# Revit family: Gymnasium-Eqpt_Basketball_IPIbybison_IP1345SF
name_source: partatom
category: Specialty Equipment
revit_build: Autodesk Revit 2018 (Build: 20170927_1515(x64)
units: mm (PartAtom-declared; Revit-internal decimal feet)

## family parameters
Always vertical = Yes
Cut with Voids When Loaded = No
Part Type = Normal
Room Calculation Point = No
Round Connector Dimension = Use Diameter
Shared = No

## types (2) — shared parameters
Available Options = as Specified
Backboard Type = Backboard_BA42XLGlass
Manufacturer = IPI by Bison
Manufacturer Fax = 800-638-0698
Manufacturer Website = https://ipibybison.com
Product Data = http://www.arcat.com
Revision = R1_01-2018
Sales Information = https://ipibybison.com
URL = https://ipibybison.com
zero-valued in all types: Expected Lifespan (Years), Maintenance Schedule (Months), Warranty Duration (Years)

## per-type parameters (varying)
| type | Description | Fold Left | Fold Right | Model |
| Right Fold | IPI by Bison Right Side Folding Basketball Frame and Backboard - IP1345SFR 23' as Specified | No | Yes | IP1345SFR 23' |
| Left Fold | IPI by Bison Left Side Folding Basketball Frame and Backboard - IP1345SFL 23' as Specified | Yes | No | IP1345SFL 23' |

## geometry (parser evidence)
native form markers: Sweep x6
no freeform markers — native parametric forms only
